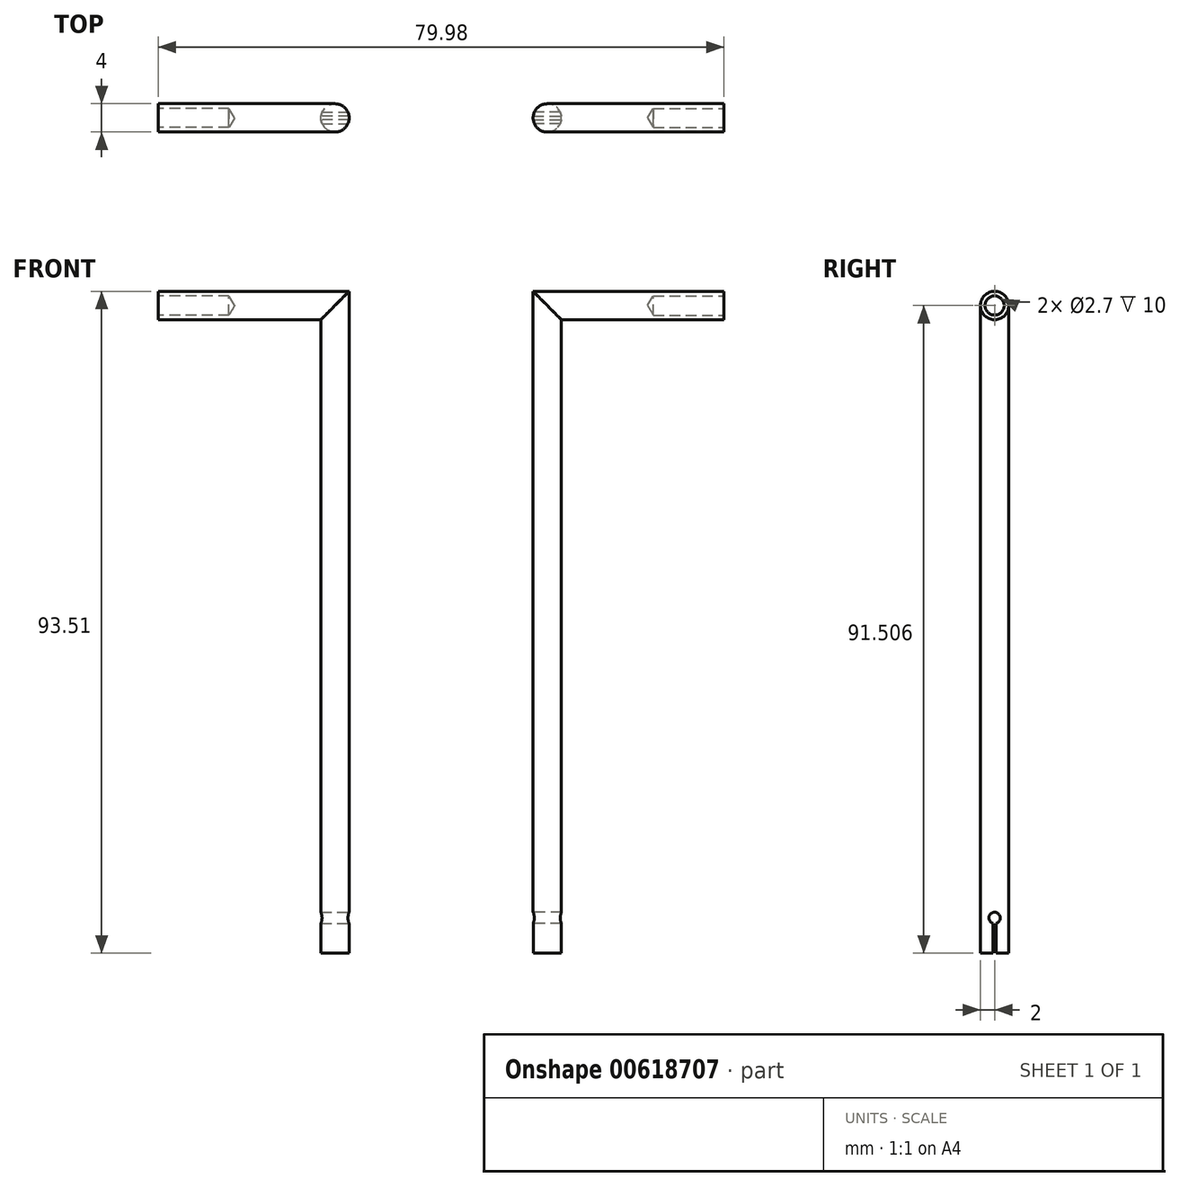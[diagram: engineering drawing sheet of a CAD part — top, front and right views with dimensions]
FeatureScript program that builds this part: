
annotation { "Feature Type Name" : "Feature", "Feature Type Description" : "" }
export const myFeature = defineFeature(function(context is Context, id is Id, definition is map)
    precondition{}
    {
        {
            var Q0;
            Q0=qCreatedBy(makeId("Top.planeOp"),FACE);
            cPlane(context, id + "F0", {"entities" : qUnion([Q0]), "cplaneType" : CPlaneType.OFFSET, "offset" : 20 * mm, "oppositeDirection" : true, "width" : 150 * mm, "height" : 150 * mm});
        }
        {
            var Q0;
            Q0=qCreatedBy(id+"F0.planeOp",FACE);
            var sketch = newSketch(context, id + "F1", { "sketchPlane" : qUnion([Q0])});
            skPoint(sketch, "E0", {"position": v(15, 0) * mm});
            skCircle(sketch, "E1", {"center": v(15, 0) * mm, "radius": 2 * mm});
            skSolve(sketch);
        }
        {
            var Q0;
            Q0=qCreatedBy(makeId("Front.planeOp"),FACE);
            var sketch = newSketch(context, id + "F2", { "sketchPlane" : qUnion([Q0])});
            skLineSegment(sketch, "E2", {"start": v(15, -20) * mm, "end": v(15, 71.5) * mm});
            skLineSegment(sketch, "E3", {"start": v(15, 71.5) * mm, "end": v(40, 71.5) * mm});
            skSolve(sketch);
        }
        {
            var Q0;
            Q0=makeQuery(id+"F1.imprint","IMPRINT",FACE,{"disambiguationData":[TD([[makeQuery(id+"F1.imprint","IMPRINT",EDGE,{"derivedFrom":sQuery(id+"F1.wireOp",EDGE,"E1")}),1.0]])]});
            var Q1;
            Q1=sQuery(id+"F2.wireOp",EDGE,"E2");
            var Q2;
            Q2=sQuery(id+"F2.wireOp",EDGE,"E3");
            sweep(context, id + "F3", {"profiles" : qUnion([Q0]), "path" : qUnion([Q1, Q2])});
        }
        {
            var Q0;
            Q0=qCreatedBy(makeId("Right.planeOp"),FACE);
            cPlane(context, id + "F4", {"entities" : qUnion([Q0]), "cplaneType" : CPlaneType.OFFSET, "offset" : 13 * mm, "width" : 150 * mm, "height" : 150 * mm});
        }
        {
            var Q0;
            Q0=qCreatedBy(id+"F4.planeOp",FACE);
            var sketch = newSketch(context, id + "F5", { "sketchPlane" : qUnion([Q0])});
            skPoint(sketch, "E4", {"position": v(0, -15) * mm});
            skSolve(sketch);
        }
        {
            var Q0;
            Q0=sQuery(id+"F5.wireOp",VERTEX,"E4");
            var Q1;
            Q1=makeQuery(id+"F3.opSweep","SWEPT_BODY",BODY,{"disambiguationData":[OSD([sQuery(id+"F1.wireOp",EDGE,"E1"),sQuery(id+"F2.wireOp",EDGE,"E3")])]});
            hole(context, id + "F6", {"style" : HoleStyle.SIMPLE, "endStyle" : HoleEndStyle.THROUGH, "oppositeDirection" : true, "holeDiameter" : 1.6 * mm, "majorDiameter" : 5 * mm, "isTappedThrough" : true, "tappedDepth" : 12 * mm, "tapClearance" : 3, "locations" : qUnion([Q0]), "scope" : qUnion([Q1])});
        }
        {
            var Q0;
            Q0=qCreatedBy(id+"F4.planeOp",FACE);
            var sketch = newSketch(context, id + "F7", { "sketchPlane" : qUnion([Q0])});
            skLineSegment(sketch, "E5.bottom", {"start": v(-0.25, -15.7) * mm, "end": v(0.25, -15.7) * mm});
            skLineSegment(sketch, "E5.top", {"start": v(-0.25, -20) * mm, "end": v(0.25, -20) * mm});
            skLineSegment(sketch, "E5.left", {"start": v(-0.25, -15.7) * mm, "end": v(-0.25, -20) * mm});
            skLineSegment(sketch, "E5.right", {"start": v(0.25, -15.7) * mm, "end": v(0.25, -20) * mm});
            skSolve(sketch);
        }
        {
            var Q0;
            Q0=qCreatedBy(makeId("Front.planeOp"),FACE);
            var sketch = newSketch(context, id + "F8", { "sketchPlane" : qUnion([Q0])});
            skLineSegment(sketch, "E6", {"start": v(12.98, -18.39) * mm, "end": v(17, -18.39) * mm});
            skSolve(sketch);
        }
        {
            var Q0;
            Q0 = qSketchRegion(id + "F7", true);
            var Q1;
            Q1 = qConstructionFilter(qBodyType(qCreatedBy(id + "F8" ,EDGE), BodyType.WIRE), ConstructionObject.NO);
            sweep(context, id + "F9", {"operationType" : NewBodyOperationType.REMOVE, "profiles" : qUnion([Q0]), "path" : qUnion([Q1])});
        }
        {
            var Q0;
            Q0=makeQuery(id+"F3.opSweep","CAP_FACE",FACE,{"disambiguationData":[OSD([sQuery(id+"F1.wireOp",EDGE,"E1"),sQuery(id+"F2.wireOp",VERTEX,"E3.end")])],"isStart":false});
            var sketch = newSketch(context, id + "F10", { "sketchPlane" : qUnion([Q0])});
            skPoint(sketch, "E7", {"position": v(0, 71.5) * mm});
            skSolve(sketch);
        }
        {
            var Q0;
            Q0=sQuery(id+"F10.wireOp",VERTEX,"E7");
            var Q1;
            Q1=makeQuery(id+"F3.opSweep","SWEPT_BODY",BODY,{"disambiguationData":[OSD([sQuery(id+"F1.wireOp",EDGE,"E1"),sQuery(id+"F2.wireOp",EDGE,"E3")])]});
            hole(context, id + "F11", {"style" : HoleStyle.SIMPLE, "endStyle" : HoleEndStyle.BLIND, "holeDiameter" : 2.7 * mm, "majorDiameter" : 5 * mm, "holeDepth" : 10 * mm, "isTappedThrough" : true, "tappedDepth" : 12 * mm, "tapClearance" : 3, "locations" : qUnion([Q0]), "scope" : qUnion([Q1])});
        }
        {
            var Q0;
            Q0=makeQuery(id+"F3.opSweep","SWEPT_BODY",BODY,{"disambiguationData":[OSD([sQuery(id+"F1.wireOp",EDGE,"E1"),sQuery(id+"F2.wireOp",EDGE,"E3")])]});
            var Q1;
            Q1=qCreatedBy(makeId("Right.planeOp"),FACE);
            mirror(context, id + "F12", {"entities" : qUnion([Q0]), "mirrorPlane" : qUnion([Q1])});
        }
    });
